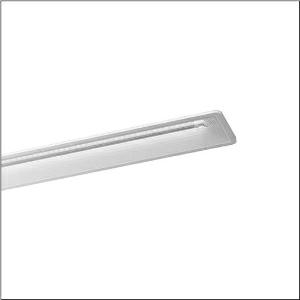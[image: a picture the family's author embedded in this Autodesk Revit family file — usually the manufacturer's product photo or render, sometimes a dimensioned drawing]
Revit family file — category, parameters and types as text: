
# Revit family: taris_r__21_5mt115d04wd_a05d
name_source: partatom
category: Lighting Fixtures
units: mm (PartAtom-declared; Revit-internal decimal feet)

## family parameters
Cut with Voids When Loaded = No
Host = Face
Light Source = No
Part Type = Normal
Room Calculation Point = No
Round Connector Dimension = Use Diameter
Shared = No

## types (1)
- --- (1 x LED, 3680 lm, 22.2 W, 4000K)
    Apparent Load = 22 VA
    CIE Flux Codes = 73 96 99 100 100
    Color Rendering = 80
    Color Temperature = 4000K
    Default Elevation = 1800 mm
    Description = Taris® 21, office luminaire, primary anti-glare with micro louvre, primary optical cover: axial lens, of PMMA, structured, CAT 2 (L<= 1500cd/m²), light emission: direct distribution, primary light characteristic: symmetric, installation type: recessed, LED, rated luminous flux: 3.680lm, luminous efficacy: 166lm/W, light colour: 840, colour temperature: 4000K, control gear: ECG DALI, with terminal, 5-pole, mains connection: 230V, AC, 50Hz, rated input power: 22W, housing, luminaire housing, of plastic, traffic white (RAL 9016), length: 968mm, width: 150mm, height: 76mm, recess depth: 106mm, protection rating (complete): IP20, insulation class (complete): insulation class I (protective earthing), certification: CE, ENEC, VDE, protection symbol: F, impact resistance: IK02, permissible operating ambient temperature: 0..+35°C, standard: EN 50419, packaging unit: 1 piece
    Height = 0 mm  [stored 0 ft]
    Lamp = 1 x LED
    Lamp Light Flux = 3680 lm
    Lamp Power = 22.2 W
    Lamp count = 1
    Length = 962 mm
    Luminous efficacy = 166 lm/W
    Manufacturer = Siteco
    ModVariant = No
    Model = 5MT115D04WD
    Mounting Place = Ceiling
    Mounting Type = Recessed
    Number of Poles = 1
    OnlyDefault = Yes
    Power Factor = 1
    Product Name = Taris® 21
    Product group = office luminaire | ceiling recessed
    ProductGroupID = 401
    Protection Class = Protection class I
    Protection Degree = IP 20
    RLX_Detail_Level = 1
    RLX_Emergency_Light_Flux = 0 lm
    RLX_Emergency_Type = 0
    RLX_Emergency_Type_DB = No
    RlxData = <blob elided: 29689 chars, md5=19307da2>
    Socket = socket
    Standby Power = 0 W
    System Light Flux = 3680 lm
    System Power = 22 W
    Type Comments = factory setting: luminous flux: 100 % | dim-lin: 254 | 200 mA
    Type Image = l_1004723.jpg
    URL = http://relux.com
    VarID = @adj_137061
    Voltage = 0 V
    Weight = 0.00 kg
    Width = 144 mm

note: [stored X ft] marks values corroborated as IEEE doubles in the binary element streams (Revit-internal decimal feet)

## geometry (parser evidence)
native form markers: Blend x4, Sweep x8
no freeform markers — native parametric forms only
